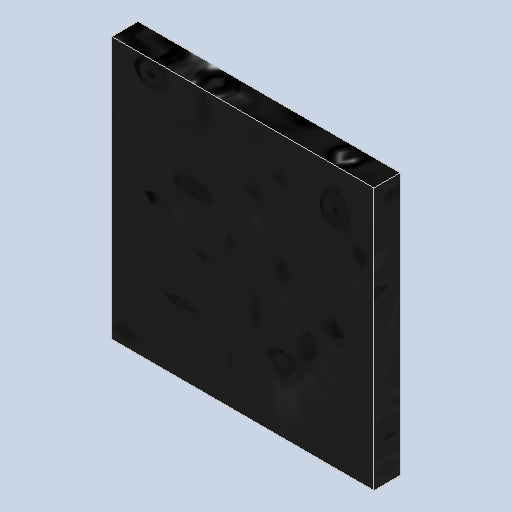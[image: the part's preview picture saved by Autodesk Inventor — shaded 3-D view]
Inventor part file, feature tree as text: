
AUTODESK INVENTOR PART (.ipt)
format: ipt  version: 2022 (Build 260153000, 153)  size: 107,008 bytes
history: native  units: mm
features: extrude x1, sketch x1
ambient origin geometry x8: Origin, YZ Plane, XZ Plane, XY Plane, X Axis, Y Axis, Z Axis, Center Point
bodies: Solid1 (feature_tree)
feature tree (2):
  extrude  "Extrusion1"  Depth=31.75mm
  sketch  "Sketch1"  dims[d0=31.75mm d1=31.75mm d2=3.175mm d3=0.0mm]
